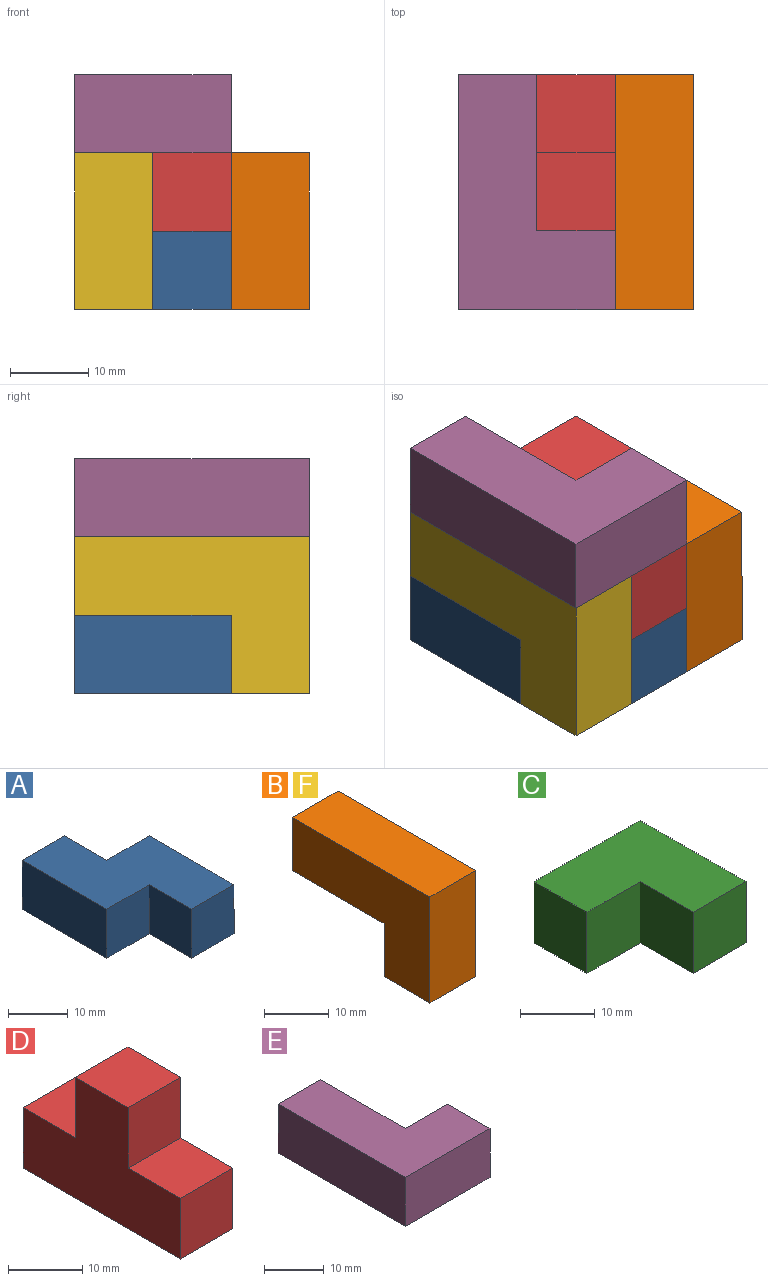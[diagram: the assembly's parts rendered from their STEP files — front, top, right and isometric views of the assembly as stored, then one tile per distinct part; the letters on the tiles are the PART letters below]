
ASSEMBLY  parts=6 mates=5
PART A: 10 faces, bbox 20x30x10 mm
  f0: plane 10x10mm, normal (0,1,0), area 100mm2, adj f2,f3,f4,f8
  f1: plane 10x10mm, normal (-1,0,0), area 100mm2, adj f2,f4,f5,f6
  f2: plane 30x20mm, normal (0,0,-1), area 400mm2, adj f0,f1,f3,f5,f6,f7,f8,f9
  f3: plane 20x10mm, normal (1,0,0), area 200mm2, adj f0,f2,f4,f5
  f4: plane 30x20mm, normal (0,0,1), area 400mm2, adj f0,f1,f3,f5,f6,f7,f8,f9
  f5: plane 10x10mm, normal (0,-1,0), area 100mm2, adj f1,f2,f3,f4
  f6: plane 10x10mm, normal (0,-1,0), area 100mm2, adj f1,f2,f4,f7
  f7: plane 20x10mm, normal (-1,0,0), area 200mm2, adj f2,f4,f6,f9
  f8: plane 10x10mm, normal (1,0,0), area 100mm2, adj f0,f2,f4,f9
  f9: plane 10x10mm, normal (0,1,0), area 100mm2, adj f2,f4,f7,f8
PART B: 8 faces, bbox 10x30x20 mm
  f0: plane 30x10mm, normal (0,0,1), area 300mm2, adj f1,f3,f4,f5
  f1: plane 30x20mm, normal (-1,0,0), area 400mm2, adj f0,f2,f4,f5,f6,f7
  f2: plane 20x10mm, normal (0,0,-1), area 200mm2, adj f1,f3,f5,f6
  f3: plane 30x20mm, normal (1,0,0), area 400mm2, adj f0,f2,f4,f5,f6,f7
  f4: plane 20x10mm, normal (0,-1,0), area 200mm2, adj f0,f1,f3,f7
  f5: plane 10x10mm, normal (0,1,0), area 100mm2, adj f0,f1,f2,f3
  f6: plane 10x10mm, normal (0,1,0), area 100mm2, adj f1,f2,f3,f7
  f7: plane 10x10mm, normal (0,0,-1), area 100mm2, adj f1,f3,f4,f6
PART C: 8 faces, bbox 20x20x10 mm
  f0: plane 20x20mm, normal (0,0,1), area 300mm2, adj f1,f3,f4,f5,f6,f7
  f1: plane 10x10mm, normal (-1,0,0), area 100mm2, adj f0,f2,f3,f4
  f2: plane 20x20mm, normal (0,0,-1), area 300mm2, adj f1,f3,f4,f5,f6,f7
  f3: plane 10x10mm, normal (0,-1,0), area 100mm2, adj f0,f1,f2,f6
  f4: plane 20x10mm, normal (0,1,0), area 200mm2, adj f0,f1,f2,f5
  f5: plane 20x10mm, normal (1,0,0), area 200mm2, adj f0,f2,f4,f7
  f6: plane 10x10mm, normal (-1,0,0), area 100mm2, adj f0,f2,f3,f7
  f7: plane 10x10mm, normal (0,-1,0), area 100mm2, adj f0,f2,f5,f6
PART D: 10 faces, bbox 10x30x20 mm
  f0: plane 10x10mm, normal (0,0,1), area 100mm2, adj f2,f4,f6,f8
  f1: plane 10x10mm, normal (0,0,1), area 100mm2, adj f2,f4,f5,f7
  f2: plane 30x20mm, normal (-1,0,0), area 400mm2, adj f0,f1,f3,f5,f6,f7,f8,f9
  f3: plane 30x10mm, normal (0,0,-1), area 300mm2, adj f2,f4,f5,f6
  f4: plane 30x20mm, normal (1,0,0), area 400mm2, adj f0,f1,f3,f5,f6,f7,f8,f9
  f5: plane 10x10mm, normal (0,-1,0), area 100mm2, adj f1,f2,f3,f4
  f6: plane 10x10mm, normal (0,1,0), area 100mm2, adj f0,f2,f3,f4
  f7: plane 10x10mm, normal (0,-1,0), area 100mm2, adj f1,f2,f4,f9
  f8: plane 10x10mm, normal (0,1,0), area 100mm2, adj f0,f2,f4,f9
  f9: plane 10x10mm, normal (0,0,1), area 100mm2, adj f2,f4,f7,f8
PART E: 8 faces, bbox 20x30x10 mm
  f0: plane 20x10mm, normal (1,0,0), area 200mm2, adj f1,f3,f5,f6
  f1: plane 30x20mm, normal (0,0,1), area 400mm2, adj f0,f2,f4,f5,f6,f7
  f2: plane 30x10mm, normal (-1,0,0), area 300mm2, adj f1,f3,f4,f5
  f3: plane 30x20mm, normal (0,0,-1), area 400mm2, adj f0,f2,f4,f5,f6,f7
  f4: plane 20x10mm, normal (0,-1,0), area 200mm2, adj f1,f2,f3,f7
  f5: plane 10x10mm, normal (0,1,0), area 100mm2, adj f0,f1,f2,f3
  f6: plane 10x10mm, normal (0,1,0), area 100mm2, adj f0,f1,f3,f7
  f7: plane 10x10mm, normal (1,0,0), area 100mm2, adj f1,f3,f4,f6
PART F: same geometry as B
PLACE A t=(-13.99,-2.63,4.33)mm
PLACE B t=(12.23,7.37,-40.18)mm
PLACE C t=(29.18,7.37,-51.54)mm
PLACE D t=(-31.18,7.37,-32.77)mm
PLACE E t=(-63.5,7.37,-25.67)mm
PLACE F t=(-7.77,7.37,-40.18)mm
MATE fastened D.f5 <-> A.f5  axis (0,-1,0) through (-18.99,-22.63,19.33)mm
MATE fastened E.f6 <-> D.f7  axis (0,1,0) through (-18.99,-12.63,29.33)mm
MATE fastened B.f6 <-> C.f7  axis (0,1,0) through (-8.99,-12.63,9.33)mm
MATE fastened C.f1 <-> A.f8  axis (-1,0,0) through (-23.99,2.37,9.33)mm
MATE fastened F.f6 <-> A.f6  axis (0,1,0) through (-28.99,-12.63,9.33)mm
